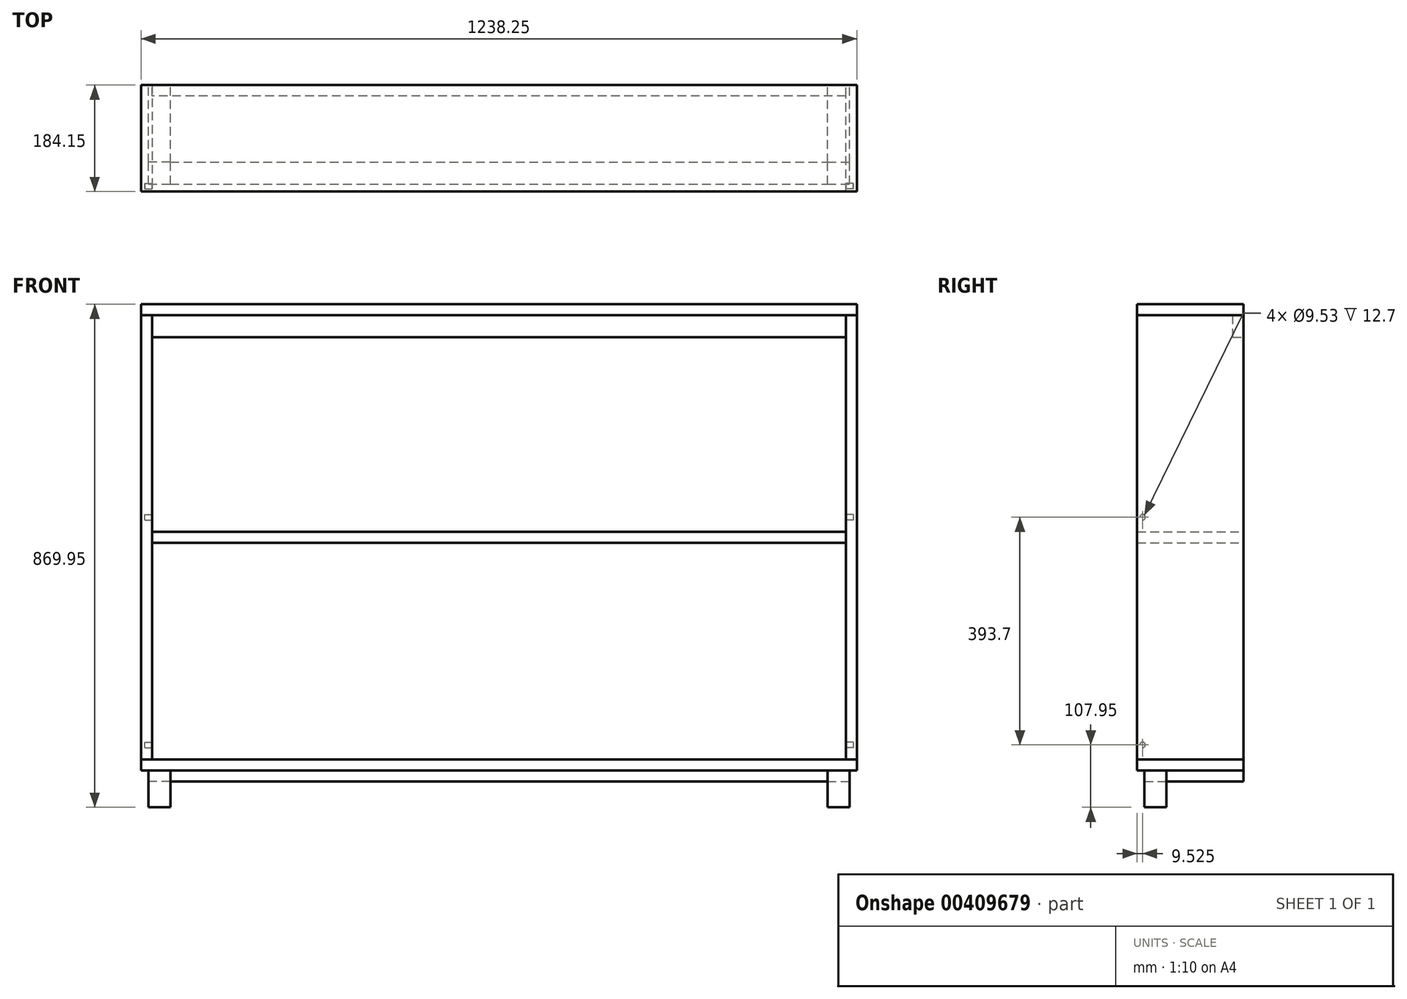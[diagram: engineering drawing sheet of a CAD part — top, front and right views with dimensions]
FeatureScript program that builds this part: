
annotation { "Feature Type Name" : "Feature", "Feature Type Description" : "" }
export const myFeature = defineFeature(function(context is Context, id is Id, definition is map)
    precondition{}
    {
        {
            var Q0;
            Q0=qCreatedBy(makeId("Top.planeOp"),FACE);
            var sketch = newSketch(context, id + "F0", { "sketchPlane" : qUnion([Q0])});
            skLineSegment(sketch, "E0.bottom", {"start": v(0, 0) * mm, "end": v(1238.25, 0) * mm});
            skLineSegment(sketch, "E0.top", {"start": v(0, 184.15) * mm, "end": v(1238.25, 184.15) * mm});
            skLineSegment(sketch, "E0.left", {"start": v(0, 0) * mm, "end": v(0, 184.15) * mm});
            skLineSegment(sketch, "E0.right", {"start": v(1238.25, 0) * mm, "end": v(1238.25, 184.15) * mm});
            skSolve(sketch);
        }
        {
            var Q0;
            Q0=makeQuery(id+"F0.imprint","IMPRINT",FACE,{"disambiguationData":[TD([[makeQuery(id+"F0.imprint","IMPRINT",EDGE,{"derivedFrom":sQuery(id+"F0.wireOp",EDGE,"E0.bottom")}),1.0]])]});
            extrude(context, id + "F1", {"entities" : qUnion([Q0]), "depth" : 19.05 * mm});
        }
        {
            var Q0;
            Q0=makeQuery(id+"F1.opExtrude","SWEPT_FACE",FACE,{"disambiguationData":[OSD([sQuery(id+"F0.wireOp",EDGE,"E0.left")])]});
            var sketch = newSketch(context, id + "F2", { "sketchPlane" : qUnion([Q0])});
            skLineSegment(sketch, "E1.bottom", {"start": v(-184.15, 787.4) * mm, "end": v(0, 787.4) * mm});
            skLineSegment(sketch, "E1.top", {"start": v(-184.15, 19.05) * mm, "end": v(0, 19.05) * mm});
            skLineSegment(sketch, "E1.left", {"start": v(-184.15, 787.4) * mm, "end": v(-184.15, 19.05) * mm});
            skLineSegment(sketch, "E1.right", {"start": v(0, 787.4) * mm, "end": v(0, 19.05) * mm});
            skSolve(sketch);
        }
        {
            var Q0;
            Q0=makeQuery(id+"F2.imprint","IMPRINT",FACE,{"disambiguationData":[TD([[makeQuery(id+"F2.imprint","IMPRINT",EDGE,{"derivedFrom":sQuery(id+"F2.wireOp",EDGE,"E1.bottom")}),-1.0]])]});
            extrude(context, id + "F3", {"entities" : qUnion([Q0]), "oppositeDirection" : true, "depth" : 19.05 * mm});
        }
        {
            var Q0;
            Q0=makeQuery(id+"F1.opExtrude","SWEPT_FACE",FACE,{"disambiguationData":[OSD([sQuery(id+"F0.wireOp",EDGE,"E0.right")])]});
            var sketch = newSketch(context, id + "F4", { "sketchPlane" : qUnion([Q0])});
            skLineSegment(sketch, "E2.bottom", {"start": v(0, 19.05) * mm, "end": v(184.15, 19.05) * mm});
            skLineSegment(sketch, "E2.top", {"start": v(0, 787.4) * mm, "end": v(184.15, 787.4) * mm});
            skLineSegment(sketch, "E2.left", {"start": v(0, 19.05) * mm, "end": v(0, 787.4) * mm});
            skLineSegment(sketch, "E2.right", {"start": v(184.15, 19.05) * mm, "end": v(184.15, 787.4) * mm});
            skSolve(sketch);
        }
        {
            var Q0;
            Q0=makeQuery(id+"F4.imprint","IMPRINT",FACE,{"disambiguationData":[TD([[makeQuery(id+"F4.imprint","IMPRINT",EDGE,{"derivedFrom":sQuery(id+"F4.wireOp",EDGE,"E2.bottom")}),1.0]])]});
            extrude(context, id + "F5", {"entities" : qUnion([Q0]), "oppositeDirection" : true, "depth" : 19.05 * mm});
        }
        {
            var Q0;
            Q0=makeQuery(id+"F3.opExtrude","SWEPT_FACE",FACE,{"disambiguationData":[OSD([sQuery(id+"F2.wireOp",EDGE,"E1.bottom")])]});
            var sketch = newSketch(context, id + "F6", { "sketchPlane" : qUnion([Q0])});
            skLineSegment(sketch, "E3.bottom", {"start": v(0, 184.15) * mm, "end": v(1238.25, 184.15) * mm});
            skLineSegment(sketch, "E3.top", {"start": v(0, 0) * mm, "end": v(1238.25, 0) * mm});
            skLineSegment(sketch, "E3.left", {"start": v(0, 184.15) * mm, "end": v(0, 0) * mm});
            skLineSegment(sketch, "E3.right", {"start": v(1238.25, 184.15) * mm, "end": v(1238.25, 0) * mm});
            skSolve(sketch);
        }
        {
            var Q0;
            {var subQ2=sQuery(id+"F6.wireOp",EDGE,"E3.right");Q0=makeQuery(id+"F6.imprint","IMPRINT",FACE,{"disambiguationData":[TD([[makeQuery(id+"F6.imprint","IMPRINT",EDGE,{"derivedFrom":subQ2}),-1.0]])]});}
            var Q1;
            {var subQ0=sQuery(id+"F6.wireOp",EDGE,"E3.left");Q1=makeQuery(id+"F6.imprint","IMPRINT",FACE,{"disambiguationData":[TD([[makeQuery(id+"F6.imprint","IMPRINT",EDGE,{"derivedFrom":subQ0}),1.0]])]});}
            extrude(context, id + "F7", {"entities" : qUnion([Q0, Q1]), "depth" : 19.05 * mm});
        }
        {
            var Q0;
            Q0=makeQuery(id+"F3.opExtrude","CAP_EDGE",EDGE,{"disambiguationData":[OSD([sQuery(id+"F2.wireOp",EDGE,"E1.right")])],"isStart":false});
            cPoint(context, id + "F8", {"entities" : qUnion([Q0]), "parameter" : 0.5});
        }
        {
            var Q0;
            Q0=qCreatedBy(makeId("Top.planeOp"),FACE);
            var Q1;
            Q1 = qCreatedBy(id + "F8" ,VERTEX);
            cPlane(context, id + "F9", {"entities" : qUnion([Q0, Q1]), "cplaneType" : CPlaneType.PLANE_POINT, "offset" : 25.4 * mm, "width" : 152.4 * mm, "height" : 152.4 * mm});
        }
        {
            var Q0;
            Q0=qCreatedBy(id+"F9.planeOp",FACE);
            var sketch = newSketch(context, id + "F10", { "sketchPlane" : qUnion([Q0])});
            skLineSegment(sketch, "E4.bottom", {"start": v(19.05, 0) * mm, "end": v(1219.2, 0) * mm});
            skLineSegment(sketch, "E4.top", {"start": v(19.05, 184.15) * mm, "end": v(1219.2, 184.15) * mm});
            skLineSegment(sketch, "E4.left", {"start": v(19.05, 0) * mm, "end": v(19.05, 184.15) * mm});
            skLineSegment(sketch, "E4.right", {"start": v(1219.2, 0) * mm, "end": v(1219.2, 184.15) * mm});
            skSolve(sketch);
        }
        {
            var Q0;
            Q0=makeQuery(id+"F10.imprint","IMPRINT",FACE,{"disambiguationData":[TD([[makeQuery(id+"F10.imprint","IMPRINT",EDGE,{"derivedFrom":sQuery(id+"F10.wireOp",EDGE,"E4.bottom")}),1.0]])]});
            extrude(context, id + "F11", {"entities" : qUnion([Q0]), "depth" : 19.05 * mm, "symmetric" : true});
        }
        {
            var Q0;
            Q0=makeQuery(id+"F3.opExtrude","SWEPT_FACE",FACE,{"disambiguationData":[OSD([sQuery(id+"F2.wireOp",EDGE,"E1.left")])]});
            var sketch = newSketch(context, id + "F12", { "sketchPlane" : qUnion([Q0])});
            skLineSegment(sketch, "E5.bottom", {"start": v(-1219.2, 787.4) * mm, "end": v(-19.05, 787.4) * mm});
            skLineSegment(sketch, "E5.top", {"start": v(-1219.2, 749.3) * mm, "end": v(-19.05, 749.3) * mm});
            skLineSegment(sketch, "E5.left", {"start": v(-1219.2, 787.4) * mm, "end": v(-1219.2, 749.3) * mm});
            skLineSegment(sketch, "E5.right", {"start": v(-19.05, 787.4) * mm, "end": v(-19.05, 749.3) * mm});
            skSolve(sketch);
        }
        {
            var Q0;
            Q0=makeQuery(id+"F12.imprint","IMPRINT",FACE,{"disambiguationData":[TD([[makeQuery(id+"F12.imprint","IMPRINT",EDGE,{"derivedFrom":sQuery(id+"F12.wireOp",EDGE,"E5.bottom")}),-1.0]])]});
            extrude(context, id + "F13", {"entities" : qUnion([Q0]), "oppositeDirection" : true, "depth" : 19.05 * mm});
        }
        {
            var Q0;
            Q0=makeQuery(id+"F1.opExtrude","CAP_FACE",FACE,{"disambiguationData":[OSD([sQuery(id+"F0.wireOp",EDGE,"E0.bottom"),sQuery(id+"F0.wireOp",EDGE,"E0.top"),sQuery(id+"F0.wireOp",EDGE,"E0.left"),sQuery(id+"F0.wireOp",EDGE,"E0.right")])],"isStart":true});
            var sketch = newSketch(context, id + "F14", { "sketchPlane" : qUnion([Q0])});
            skLineSegment(sketch, "E6.bottom", {"start": v(12.7, -12.7) * mm, "end": v(50.8, -12.7) * mm});
            skLineSegment(sketch, "E6.top", {"start": v(12.7, -50.8) * mm, "end": v(50.8, -50.8) * mm});
            skLineSegment(sketch, "E6.left", {"start": v(12.7, -12.7) * mm, "end": v(12.7, -50.8) * mm});
            skLineSegment(sketch, "E6.right", {"start": v(50.8, -12.7) * mm, "end": v(50.8, -50.8) * mm});
            skSolve(sketch);
        }
        {
            var Q0;
            Q0=makeQuery(id+"F14.imprint","IMPRINT",FACE,{"disambiguationData":[TD([[makeQuery(id+"F14.imprint","IMPRINT",EDGE,{"derivedFrom":sQuery(id+"F14.wireOp",EDGE,"E6.bottom")}),-1.0]])]});
            extrude(context, id + "F15", {"entities" : qUnion([Q0]), "depth" : 63.5 * mm});
        }
        {
            var Q0;
            Q0=makeQuery(id+"F1.opExtrude","CAP_FACE",FACE,{"disambiguationData":[OSD([sQuery(id+"F0.wireOp",EDGE,"E0.bottom"),sQuery(id+"F0.wireOp",EDGE,"E0.top"),sQuery(id+"F0.wireOp",EDGE,"E0.left"),sQuery(id+"F0.wireOp",EDGE,"E0.right")])],"isStart":true});
            var sketch = newSketch(context, id + "F16", { "sketchPlane" : qUnion([Q0])});
            skLineSegment(sketch, "E7.bottom", {"start": v(1187.45, -12.7) * mm, "end": v(1225.55, -12.7) * mm});
            skLineSegment(sketch, "E7.top", {"start": v(1187.45, -50.8) * mm, "end": v(1225.55, -50.8) * mm});
            skLineSegment(sketch, "E7.left", {"start": v(1187.45, -12.7) * mm, "end": v(1187.45, -50.8) * mm});
            skLineSegment(sketch, "E7.right", {"start": v(1225.55, -12.7) * mm, "end": v(1225.55, -50.8) * mm});
            skSolve(sketch);
        }
        {
            var Q0;
            Q0=makeQuery(id+"F16.imprint","IMPRINT",FACE,{"disambiguationData":[TD([[makeQuery(id+"F16.imprint","IMPRINT",EDGE,{"derivedFrom":sQuery(id+"F16.wireOp",EDGE,"E7.bottom")}),-1.0]])]});
            var Q1;
            Q1=makeQuery(id+"F15.opExtrude","CAP_FACE",FACE,{"disambiguationData":[OSD([sQuery(id+"F14.wireOp",EDGE,"E6.bottom"),sQuery(id+"F14.wireOp",EDGE,"E6.top"),sQuery(id+"F14.wireOp",EDGE,"E6.left"),sQuery(id+"F14.wireOp",EDGE,"E6.right")])],"isStart":false});
            extrude(context, id + "F17", {"entities" : qUnion([Q0]), "endBound" : BoundingType.UP_TO_SURFACE, "endBoundEntityFace" : qUnion([Q1]), "depth" : 25.4 * mm});
        }
        {
            var Q0;
            Q0=makeQuery(id+"F1.opExtrude","CAP_FACE",FACE,{"disambiguationData":[OSD([sQuery(id+"F0.wireOp",EDGE,"E0.bottom"),sQuery(id+"F0.wireOp",EDGE,"E0.top"),sQuery(id+"F0.wireOp",EDGE,"E0.left"),sQuery(id+"F0.wireOp",EDGE,"E0.right")])],"isStart":true});
            var sketch = newSketch(context, id + "F18", { "sketchPlane" : qUnion([Q0])});
            skLineSegment(sketch, "E8.bottom", {"start": v(50.8, -12.7) * mm, "end": v(1187.45, -12.7) * mm});
            skLineSegment(sketch, "E8.top", {"start": v(50.8, -50.8) * mm, "end": v(1187.45, -50.8) * mm});
            skLineSegment(sketch, "E8.left", {"start": v(50.8, -12.7) * mm, "end": v(50.8, -50.8) * mm});
            skLineSegment(sketch, "E8.right", {"start": v(1187.45, -12.7) * mm, "end": v(1187.45, -50.8) * mm});
            skSolve(sketch);
        }
        {
            var Q0;
            Q0=makeQuery(id+"F18.imprint","IMPRINT",FACE,{"disambiguationData":[TD([[makeQuery(id+"F18.imprint","IMPRINT",EDGE,{"derivedFrom":sQuery(id+"F18.wireOp",EDGE,"E8.bottom")}),-1.0]])]});
            extrude(context, id + "F19", {"entities" : qUnion([Q0]), "depth" : 19.05 * mm});
        }
        {
            var Q0;
            Q0=makeQuery(id+"F1.opExtrude","CAP_FACE",FACE,{"disambiguationData":[OSD([sQuery(id+"F0.wireOp",EDGE,"E0.bottom"),sQuery(id+"F0.wireOp",EDGE,"E0.top"),sQuery(id+"F0.wireOp",EDGE,"E0.left"),sQuery(id+"F0.wireOp",EDGE,"E0.right")])],"isStart":true});
            var sketch = newSketch(context, id + "F20", { "sketchPlane" : qUnion([Q0])});
            skLineSegment(sketch, "E9.bottom", {"start": v(50.8, -50.8) * mm, "end": v(12.7, -50.8) * mm});
            skLineSegment(sketch, "E9.top", {"start": v(50.8, -184.15) * mm, "end": v(12.7, -184.15) * mm});
            skLineSegment(sketch, "E9.left", {"start": v(50.8, -50.8) * mm, "end": v(50.8, -184.15) * mm});
            skLineSegment(sketch, "E9.right", {"start": v(12.7, -50.8) * mm, "end": v(12.7, -184.15) * mm});
            skSolve(sketch);
        }
        {
            var Q0;
            Q0=makeQuery(id+"F20.imprint","IMPRINT",FACE,{"disambiguationData":[TD([[makeQuery(id+"F20.imprint","IMPRINT",EDGE,{"derivedFrom":sQuery(id+"F20.wireOp",EDGE,"E9.bottom")}),1.0]])]});
            extrude(context, id + "F21", {"entities" : qUnion([Q0]), "depth" : 19.05 * mm});
        }
        {
            var Q0;
            Q0=makeQuery(id+"F1.opExtrude","CAP_FACE",FACE,{"disambiguationData":[OSD([sQuery(id+"F0.wireOp",EDGE,"E0.bottom"),sQuery(id+"F0.wireOp",EDGE,"E0.top"),sQuery(id+"F0.wireOp",EDGE,"E0.left"),sQuery(id+"F0.wireOp",EDGE,"E0.right")])],"isStart":true});
            var sketch = newSketch(context, id + "F22", { "sketchPlane" : qUnion([Q0])});
            skLineSegment(sketch, "E10.bottom", {"start": v(1187.45, -50.8) * mm, "end": v(1225.55, -50.8) * mm});
            skLineSegment(sketch, "E10.top", {"start": v(1187.45, -184.15) * mm, "end": v(1225.55, -184.15) * mm});
            skLineSegment(sketch, "E10.left", {"start": v(1187.45, -50.8) * mm, "end": v(1187.45, -184.15) * mm});
            skLineSegment(sketch, "E10.right", {"start": v(1225.55, -50.8) * mm, "end": v(1225.55, -184.15) * mm});
            skSolve(sketch);
        }
        {
            var Q0;
            Q0=makeQuery(id+"F22.imprint","IMPRINT",FACE,{"disambiguationData":[TD([[makeQuery(id+"F22.imprint","IMPRINT",EDGE,{"derivedFrom":sQuery(id+"F22.wireOp",EDGE,"E10.bottom")}),-1.0]])]});
            extrude(context, id + "F23", {"entities" : qUnion([Q0]), "depth" : 19.05 * mm});
        }
        {
            var Q0;
            Q0=makeQuery(id+"F3.opExtrude","CAP_FACE",FACE,{"disambiguationData":[OSD([sQuery(id+"F2.wireOp",EDGE,"E1.bottom"),sQuery(id+"F2.wireOp",EDGE,"E1.top"),sQuery(id+"F2.wireOp",EDGE,"E1.left"),sQuery(id+"F2.wireOp",EDGE,"E1.right")])],"isStart":false});
            var sketch = newSketch(context, id + "F24", { "sketchPlane" : qUnion([Q0])});
            skCircle(sketch, "E11", {"center": v(9.53, 438.15) * mm, "radius": 4.76 * mm});
            skSolve(sketch);
        }
        {
            var Q0;
            Q0=makeQuery(id+"F24.imprint","IMPRINT",FACE,{"disambiguationData":[TD([[makeQuery(id+"F24.imprint","IMPRINT",EDGE,{"derivedFrom":sQuery(id+"F24.wireOp",EDGE,"E11")}),1.0]])]});
            extrude(context, id + "F25", {"entities" : qUnion([Q0]), "operationType" : NewBodyOperationType.REMOVE, "oppositeDirection" : true, "depth" : 12.7 * mm});
        }
        {
            var Q0;
            Q0=makeQuery(id+"F5.opExtrude","CAP_FACE",FACE,{"disambiguationData":[OSD([sQuery(id+"F4.wireOp",EDGE,"E2.bottom"),sQuery(id+"F4.wireOp",EDGE,"E2.top"),sQuery(id+"F4.wireOp",EDGE,"E2.left"),sQuery(id+"F4.wireOp",EDGE,"E2.right")])],"isStart":false});
            var sketch = newSketch(context, id + "F26", { "sketchPlane" : qUnion([Q0])});
            skCircle(sketch, "E12", {"center": v(-9.52, 438.15) * mm, "radius": 4.76 * mm});
            skSolve(sketch);
        }
        {
            var Q0;
            Q0=makeQuery(id+"F26.imprint","IMPRINT",FACE,{"disambiguationData":[TD([[makeQuery(id+"F26.imprint","IMPRINT",EDGE,{"derivedFrom":sQuery(id+"F26.wireOp",EDGE,"E12")}),1.0]])]});
            extrude(context, id + "F27", {"entities" : qUnion([Q0]), "operationType" : NewBodyOperationType.REMOVE, "oppositeDirection" : true, "depth" : 12.7 * mm});
        }
        {
            var Q0;
            Q0=makeQuery(id+"F3.opExtrude","CAP_FACE",FACE,{"disambiguationData":[OSD([sQuery(id+"F2.wireOp",EDGE,"E1.bottom"),sQuery(id+"F2.wireOp",EDGE,"E1.top"),sQuery(id+"F2.wireOp",EDGE,"E1.left"),sQuery(id+"F2.wireOp",EDGE,"E1.right")])],"isStart":false});
            var sketch = newSketch(context, id + "F28", { "sketchPlane" : qUnion([Q0])});
            skCircle(sketch, "E13", {"center": v(9.52, 44.45) * mm, "radius": 4.76 * mm});
            skSolve(sketch);
        }
        {
            var Q0;
            Q0=makeQuery(id+"F28.imprint","IMPRINT",FACE,{"disambiguationData":[TD([[makeQuery(id+"F28.imprint","IMPRINT",EDGE,{"derivedFrom":sQuery(id+"F28.wireOp",EDGE,"E13")}),1.0]])]});
            extrude(context, id + "F29", {"entities" : qUnion([Q0]), "operationType" : NewBodyOperationType.REMOVE, "oppositeDirection" : true, "depth" : 12.7 * mm});
        }
        {
            var Q0;
            Q0=makeQuery(id+"F5.opExtrude","CAP_FACE",FACE,{"disambiguationData":[OSD([sQuery(id+"F4.wireOp",EDGE,"E2.bottom"),sQuery(id+"F4.wireOp",EDGE,"E2.top"),sQuery(id+"F4.wireOp",EDGE,"E2.left"),sQuery(id+"F4.wireOp",EDGE,"E2.right")])],"isStart":false});
            var sketch = newSketch(context, id + "F30", { "sketchPlane" : qUnion([Q0])});
            skCircle(sketch, "E14", {"center": v(-9.52, 44.45) * mm, "radius": 4.76 * mm});
            skSolve(sketch);
        }
        {
            var Q0;
            Q0=makeQuery(id+"F30.imprint","IMPRINT",FACE,{"disambiguationData":[TD([[makeQuery(id+"F30.imprint","IMPRINT",EDGE,{"derivedFrom":sQuery(id+"F30.wireOp",EDGE,"E14")}),1.0]])]});
            extrude(context, id + "F31", {"entities" : qUnion([Q0]), "operationType" : NewBodyOperationType.REMOVE, "oppositeDirection" : true, "depth" : 12.7 * mm});
        }
    });
